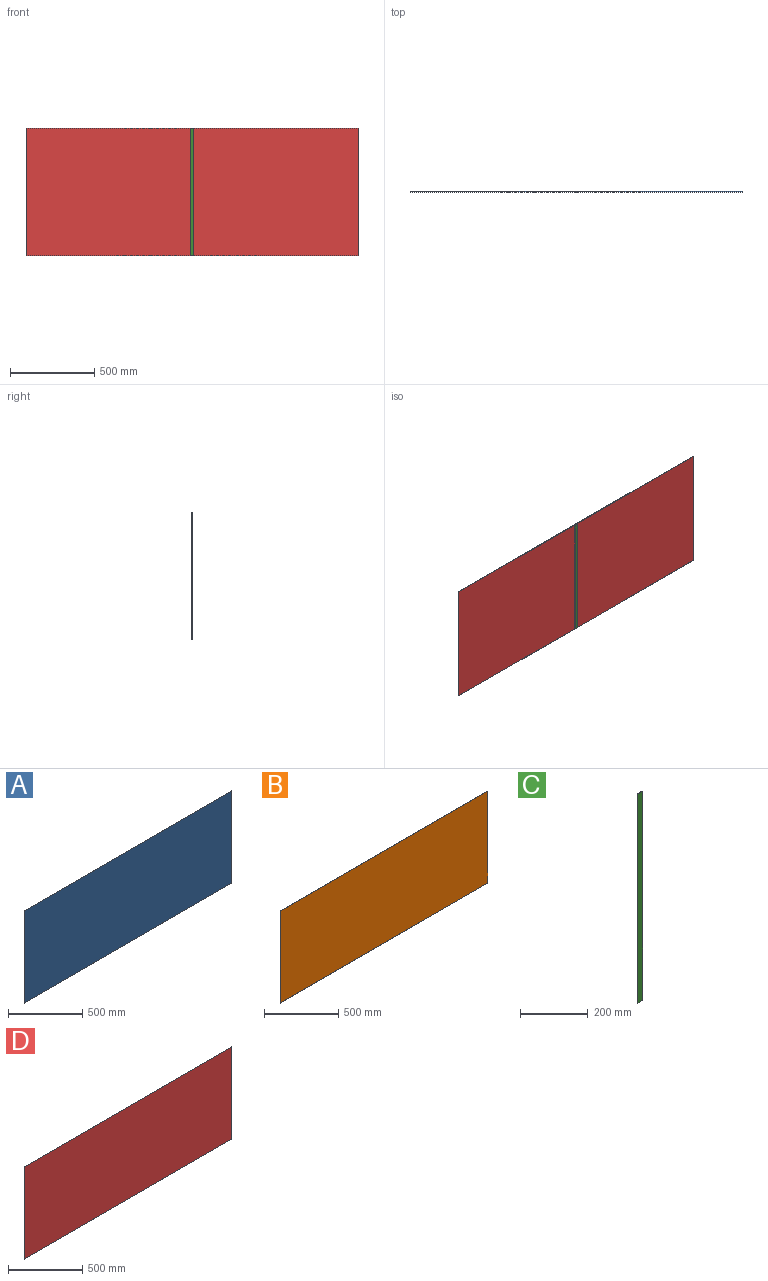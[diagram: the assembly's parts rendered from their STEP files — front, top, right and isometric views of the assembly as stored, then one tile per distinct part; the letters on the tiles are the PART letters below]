
ASSEMBLY  parts=4 mates=1
PART A: 6 faces, bbox 1975x0.3x757 mm
  f0: plane 757x0.25mm, normal (1,0,0), area 189.2mm2, adj f1,f3,f4,f5
  f1: plane 1975x0.25mm, normal (0,0,1), area 493.8mm2, adj f0,f2,f4,f5
  f2: plane 757x0.25mm, normal (-1,0,0), area 189.2mm2, adj f1,f3,f4,f5
  f3: plane 1975x0.25mm, normal (0,0,-1), area 493.8mm2, adj f0,f2,f4,f5
  f4: plane 1975x757mm, normal (0,-1,0), area 1495075mm2, adj f0,f1,f2,f3
  f5: plane 1975x757mm, normal (0,1,0), area 1495075mm2, adj f0,f1,f2,f3
PART B: 6 faces, bbox 1975x2.5x757 mm
  f0: plane 757x2.5mm, normal (1,0,0), area 1892.5mm2, adj f1,f3,f4,f5
  f1: plane 1975x2.5mm, normal (0,0,1), area 4937.5mm2, adj f0,f2,f4,f5
  f2: plane 757x2.5mm, normal (-1,0,0), area 1892.5mm2, adj f1,f3,f4,f5
  f3: plane 1975x2.5mm, normal (0,0,-1), area 4937.5mm2, adj f0,f2,f4,f5
  f4: plane 1975x757mm, normal (0,-1,0), area 1495075mm2, adj f0,f1,f2,f3
  f5: plane 1975x757mm, normal (0,1,0), area 1495075mm2, adj f0,f1,f2,f3
PART C: 6 faces, bbox 20x2x757 mm
  f0: plane 20x2mm, normal (0,0,1), area 40mm2, adj f1,f3,f4,f5
  f1: plane 757x20mm, normal (0,1,0), area 15140mm2, adj f0,f2,f3,f4
  f2: plane 20x2mm, normal (0,0,-1), area 40mm2, adj f1,f3,f4,f5
  f3: plane 757x2mm, normal (-1,0,0), area 1514mm2, adj f0,f1,f2,f5
  f4: plane 757x2mm, normal (1,0,0), area 1514mm2, adj f0,f1,f2,f5
  f5: plane 757x20mm, normal (0,-1,0), area 15140mm2, adj f0,f2,f3,f4
PART D: 6 faces, bbox 1975x0.3x757 mm
  f0: plane 757x0.25mm, normal (1,0,0), area 189.3mm2, adj f1,f3,f4,f5
  f1: plane 1975x0.25mm, normal (0,0,1), area 493.8mm2, adj f0,f2,f4,f5
  f2: plane 757x0.25mm, normal (-1,0,0), area 189.3mm2, adj f1,f3,f4,f5
  f3: plane 1975x0.25mm, normal (0,0,-1), area 493.8mm2, adj f0,f2,f4,f5
  f4: plane 1975x757mm, normal (0,-1,0), area 1495075mm2, adj f0,f1,f2,f3
  f5: plane 1975x757mm, normal (0,1,0), area 1495075mm2, adj f0,f1,f2,f3
PLACE A rot(axis=(0.02,0.13,-0.99),0deg) t=(8.12,1.5,-359.75)mm
PLACE B rot(axis=(0.02,0.13,-0.99),0deg) t=(8.12,1.5,-359.75)mm
PLACE C rot(axis=(0.03,-0.02,-1),0deg) t=(335.62,1.5,-359.75)mm
PLACE D rot(axis=(0.02,0.13,-0.99),0deg) t=(8.12,1.5,-359.75)mm
MATE fastened C.f1 <-> D.f4  axis (0,1,0) through (8.12,-1.5,18.75)mm
